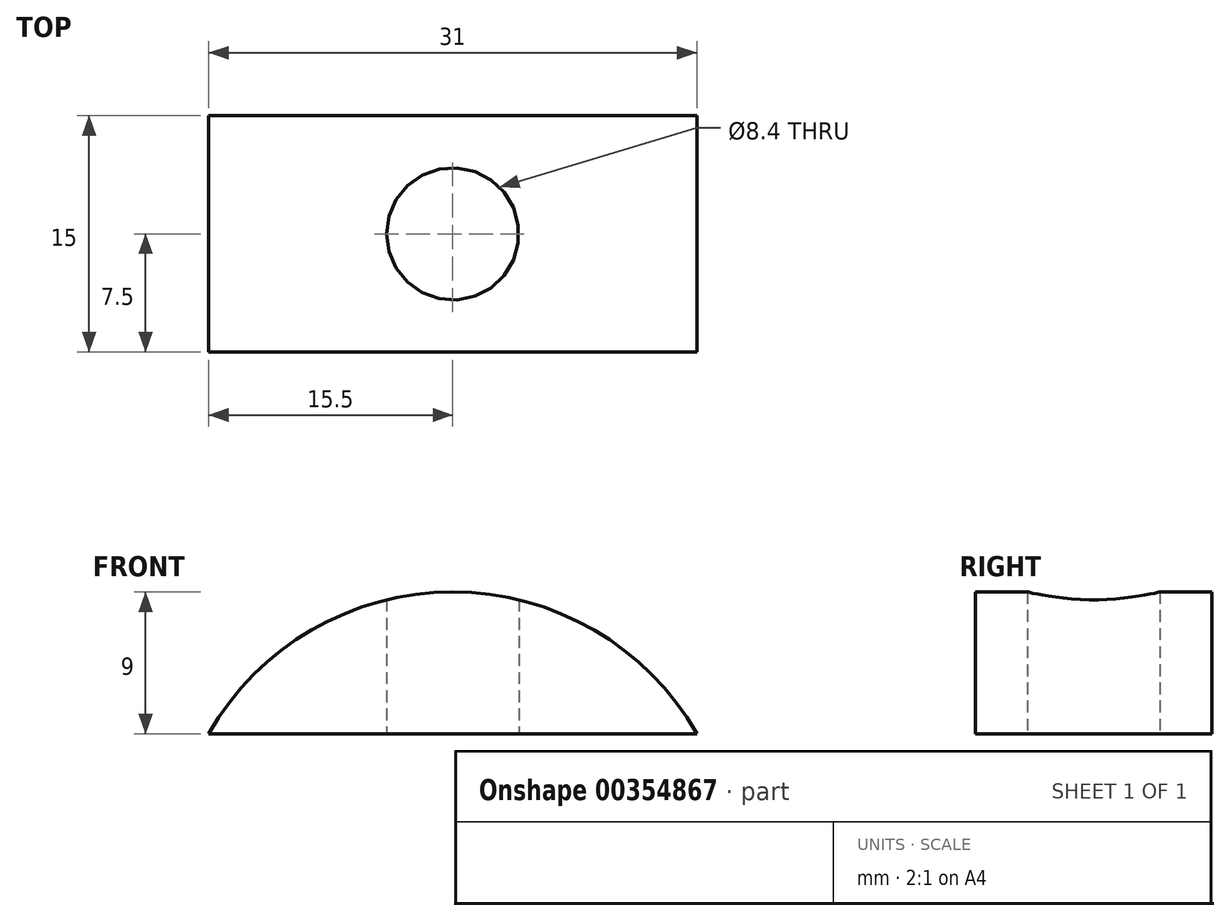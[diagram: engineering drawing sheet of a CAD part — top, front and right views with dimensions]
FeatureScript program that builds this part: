
annotation { "Feature Type Name" : "Feature", "Feature Type Description" : "" }
export const myFeature = defineFeature(function(context is Context, id is Id, definition is map)
    precondition{}
    {
        {
            var Q0;
            Q0=qCreatedBy(makeId("Front.planeOp"),FACE);
            var sketch = newSketch(context, id + "F0", { "sketchPlane" : qUnion([Q0])});
            skArc(sketch, "E0", {"start": v(15.5, 32.74) * mm, "mid": v(0, 41.74) * mm, "end": v(-15.5, 32.74) * mm});
            skLineSegment(sketch, "E1", {"start": v(-15.5, 32.74) * mm, "end": v(0, 32.74) * mm});
            skLineSegment(sketch, "E2", {"start": v(0, 32.74) * mm, "end": v(15.5, 32.74) * mm});
            skPoint(sketch, "E3", {"position": v(0, 41.74) * mm});
            skSolve(sketch);
        }
        {
            var Q0;
            Q0=makeQuery(id+"F0.imprint","IMPRINT",FACE,{"disambiguationData":[TD([[makeQuery(id+"F0.imprint","IMPRINT",EDGE,{"derivedFrom":sQuery(id+"F0.wireOp",EDGE,"E0")}),1.0]])]});
            extrude(context, id + "F1", {"entities" : qUnion([Q0]), "oppositeDirection" : true, "depth" : 15 * mm});
        }
        {
            var Q0;
            Q0=makeQuery(id+"F1.opExtrude","SWEPT_FACE",FACE,{"disambiguationData":[OSD([sQuery(id+"F0.wireOp",EDGE,"E1"),sQuery(id+"F0.wireOp",EDGE,"E2")])]});
            var sketch = newSketch(context, id + "F2", { "sketchPlane" : qUnion([Q0])});
            skCircle(sketch, "E4", {"center": v(0, -7.5) * mm, "radius": 4.2 * mm});
            skSolve(sketch);
        }
        {
            var Q0;
            Q0 = qSketchRegion(id + "F2", true);
            extrude(context, id + "F3", {"entities" : qUnion([Q0]), "operationType" : NewBodyOperationType.REMOVE, "oppositeDirection" : true, "depth" : 25 * mm});
        }
    });
